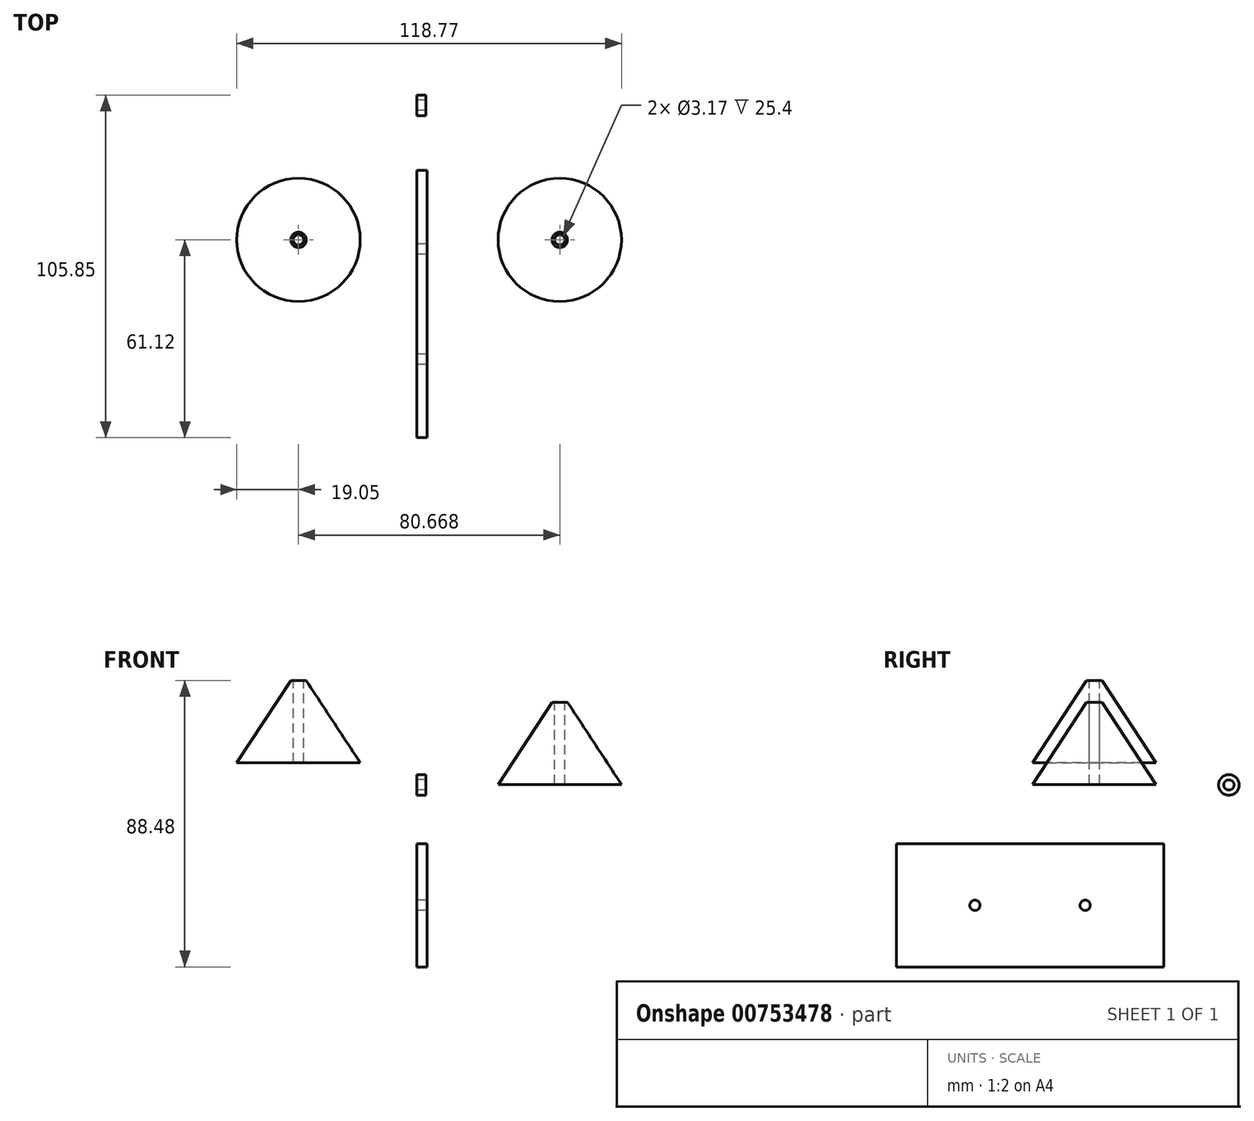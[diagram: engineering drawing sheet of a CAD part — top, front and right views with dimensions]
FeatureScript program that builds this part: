
annotation { "Feature Type Name" : "Feature", "Feature Type Description" : "" }
export const myFeature = defineFeature(function(context is Context, id is Id, definition is map)
    precondition{}
    {
        {
            var Q0;
            Q0=qCreatedBy(makeId("Front.planeOp"),FACE);
            var sketch = newSketch(context, id + "F0", { "sketchPlane" : qUnion([Q0])});
            skLineSegment(sketch, "E0", {"start": v(-38.88, 58.36) * mm, "end": v(-36.5, 58.36) * mm});
            skLineSegment(sketch, "E1", {"start": v(-36.5, 58.36) * mm, "end": v(-36.5, 32.96) * mm});
            skLineSegment(sketch, "E2", {"start": v(-36.5, 32.96) * mm, "end": v(-55.55, 32.96) * mm});
            skLineSegment(sketch, "E3", {"start": v(-38.88, 58.36) * mm, "end": v(-55.55, 32.96) * mm});
            skLineSegment(sketch, "E4", {"start": v(44.17, 51.66) * mm, "end": v(41.79, 51.66) * mm});
            skLineSegment(sketch, "E5", {"start": v(44.17, 51.66) * mm, "end": v(44.17, 26.26) * mm});
            skLineSegment(sketch, "E6", {"start": v(44.17, 26.26) * mm, "end": v(25.12, 26.26) * mm});
            skLineSegment(sketch, "E7", {"start": v(41.79, 51.66) * mm, "end": v(25.12, 26.26) * mm});
            skSolve(sketch);
        }
        {
            var Q0;
            Q0=makeQuery(id+"F0.imprint","IMPRINT",FACE,{"disambiguationData":[TD([[makeQuery(id+"F0.imprint","IMPRINT",EDGE,{"derivedFrom":sQuery(id+"F0.wireOp",EDGE,"E0")}),-1.0]])]});
            var Q1;
            Q1=sQuery(id+"F0.wireOp",EDGE,"E1");
            revolve(context, id + "F1", {"surfaceOperationType" : NewSurfaceOperationType.NEW, "entities" : qUnion([Q0]), "axis" : qUnion([Q1]), "revolveType" : RevolveType.FULL});
        }
        {
            var Q0;
            Q0=makeQuery(id+"F0.imprint","IMPRINT",FACE,{"disambiguationData":[TD([[makeQuery(id+"F0.imprint","IMPRINT",EDGE,{"derivedFrom":sQuery(id+"F0.wireOp",EDGE,"E4")}),1.0]])]});
            var Q1;
            Q1=sQuery(id+"F0.wireOp",EDGE,"E5");
            revolve(context, id + "F2", {"surfaceOperationType" : NewSurfaceOperationType.NEW, "entities" : qUnion([Q0]), "axis" : qUnion([Q1]), "revolveType" : RevolveType.FULL});
        }
        {
            var Q0;
            Q0=makeQuery(id+"F1.opRevolve","SWEPT_FACE",FACE,{"disambiguationData":[OSD([sQuery(id+"F0.wireOp",EDGE,"E0")])]});
            var sketch = newSketch(context, id + "F3", { "sketchPlane" : qUnion([Q0])});
            skCircle(sketch, "E8", {"center": v(-36.5, 0) * mm, "radius": 1.59 * mm});
            skSolve(sketch);
        }
        {
            var Q0;
            Q0=makeQuery(id+"F3.imprint","IMPRINT",FACE,{"disambiguationData":[TD([[makeQuery(id+"F3.imprint","IMPRINT",EDGE,{"derivedFrom":sQuery(id+"F3.wireOp",EDGE,"E8")}),1.0]])]});
            extrude(context, id + "F4", {"entities" : qUnion([Q0]), "operationType" : NewBodyOperationType.REMOVE, "oppositeDirection" : true, "depth" : 25.9 * mm, "offsetDistance" : 25.4 * mm});
        }
        {
            var Q0;
            Q0=makeQuery(id+"F2.opRevolve","SWEPT_FACE",FACE,{"disambiguationData":[OSD([sQuery(id+"F0.wireOp",EDGE,"E4")])]});
            var sketch = newSketch(context, id + "F5", { "sketchPlane" : qUnion([Q0])});
            skCircle(sketch, "E9", {"center": v(44.17, 0) * mm, "radius": 1.59 * mm});
            skSolve(sketch);
        }
        {
            var Q0;
            Q0=makeQuery(id+"F5.imprint","IMPRINT",FACE,{"disambiguationData":[TD([[makeQuery(id+"F5.imprint","IMPRINT",EDGE,{"derivedFrom":sQuery(id+"F5.wireOp",EDGE,"E9")}),1.0]])]});
            extrude(context, id + "F6", {"entities" : qUnion([Q0]), "operationType" : NewBodyOperationType.REMOVE, "oppositeDirection" : true, "depth" : 25.4 * mm, "offsetDistance" : 25.4 * mm});
        }
        {
            var Q0;
            Q0=qCreatedBy(makeId("Right.planeOp"),FACE);
            var sketch = newSketch(context, id + "F7", { "sketchPlane" : qUnion([Q0])});
            skCircle(sketch, "E10", {"center": v(-54.36, 25.77) * mm, "radius": 1.59 * mm});
            skCircle(sketch, "E11", {"center": v(41.55, 26.1) * mm, "radius": 1.59 * mm});
            skCircle(sketch, "E12", {"center": v(41.55, 26.1) * mm, "radius": 3.18 * mm});
            skSolve(sketch);
        }
        {
            var Q0;
            Q0=makeQuery(id+"F7.imprint","IMPRINT",FACE,{"disambiguationData":[TD([[makeQuery(id+"F7.imprint","IMPRINT",EDGE,{"derivedFrom":sQuery(id+"F7.wireOp",EDGE,"E11")}),-1.0]])]});
            extrude(context, id + "F8", {"entities" : qUnion([Q0]), "depth" : 2.77 * mm, "offsetDistance" : 25.4 * mm});
        }
        {
            var Q0;
            Q0=qCreatedBy(makeId("Right.planeOp"),FACE);
            var sketch = newSketch(context, id + "F9", { "sketchPlane" : qUnion([Q0])});
            skLineSegment(sketch, "E13.bottom", {"start": v(-61.12, 7.98) * mm, "end": v(21.43, 7.98) * mm});
            skLineSegment(sketch, "E13.top", {"start": v(-61.12, -30.12) * mm, "end": v(21.43, -30.12) * mm});
            skLineSegment(sketch, "E13.left", {"start": v(-61.12, 7.98) * mm, "end": v(-61.12, -30.12) * mm});
            skLineSegment(sketch, "E13.right", {"start": v(21.43, 7.98) * mm, "end": v(21.43, -30.12) * mm});
            skLineSegment(sketch, "E14.bottom", {"start": v(-19.44, 26.43) * mm, "end": v(18.66, 26.43) * mm});
            skLineSegment(sketch, "E14.top", {"start": v(-19.44, 51.83) * mm, "end": v(18.66, 51.83) * mm});
            skLineSegment(sketch, "E14.left", {"start": v(-19.44, 26.43) * mm, "end": v(-19.44, 51.83) * mm});
            skLineSegment(sketch, "E14.right", {"start": v(18.66, 26.43) * mm, "end": v(18.66, 51.83) * mm});
            skCircle(sketch, "E15", {"center": v(-36.86, -11.07) * mm, "radius": 1.59 * mm});
            skCircle(sketch, "E16", {"center": v(-2.82, -11.07) * mm, "radius": 1.59 * mm});
            skPoint(sketch, "E17", {"position": v(-61.12, -11.07) * mm});
            skPoint(sketch, "E18", {"position": v(21.43, -11.07) * mm});
            skLineSegment(sketch, "E19", {"start": v(-61.12, -11.07) * mm, "end": v(-36.86, -11.07) * mm, "construction": true});
            skLineSegment(sketch, "E20", {"start": v(21.43, -11.07) * mm, "end": v(-2.82, -11.07) * mm, "construction": true});
            skSolve(sketch);
        }
        {
            var Q0;
            Q0=makeQuery(id+"F9.imprint","IMPRINT",FACE,{"disambiguationData":[TD([[makeQuery(id+"F9.imprint","IMPRINT",EDGE,{"derivedFrom":sQuery(id+"F9.wireOp",EDGE,"E13.bottom")}),-1.0]])]});
            extrude(context, id + "F10", {"entities" : qUnion([Q0]), "depth" : 3.17 * mm, "offsetDistance" : 25.4 * mm});
        }
    });
